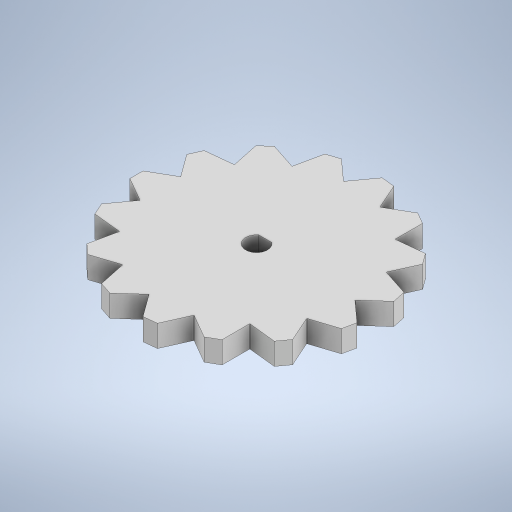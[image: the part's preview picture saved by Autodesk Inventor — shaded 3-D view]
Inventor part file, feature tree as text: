
AUTODESK INVENTOR PART (.ipt)
format: ipt  version: 2023 (Build 270158000, 158)  size: 336,384 bytes
history: native  units: in
note: dims shown in document units (in); Inventor stores cm internally (conversion verified against a paired STEP export)
features: extrude x1, sketch x1
ambient origin geometry x8: Origin, YZ Plane, XZ Plane, XY Plane, X Axis, Y Axis, Z Axis, Center Point
bodies: Solid1 (feature_tree)
feature tree (2):
  extrude  "Extrusion1"  Depth=0.1969in
  sketch  "Sketch1"  dims[d0=1.7717in d1=0.1969in d2=0.1772in d3=0.2953in d4=30.0deg d5=150.0deg d6=0.1181in d7=0.1181in d12=0.1969in d13=0.0in d22=5.9055in d24=360.0deg]
